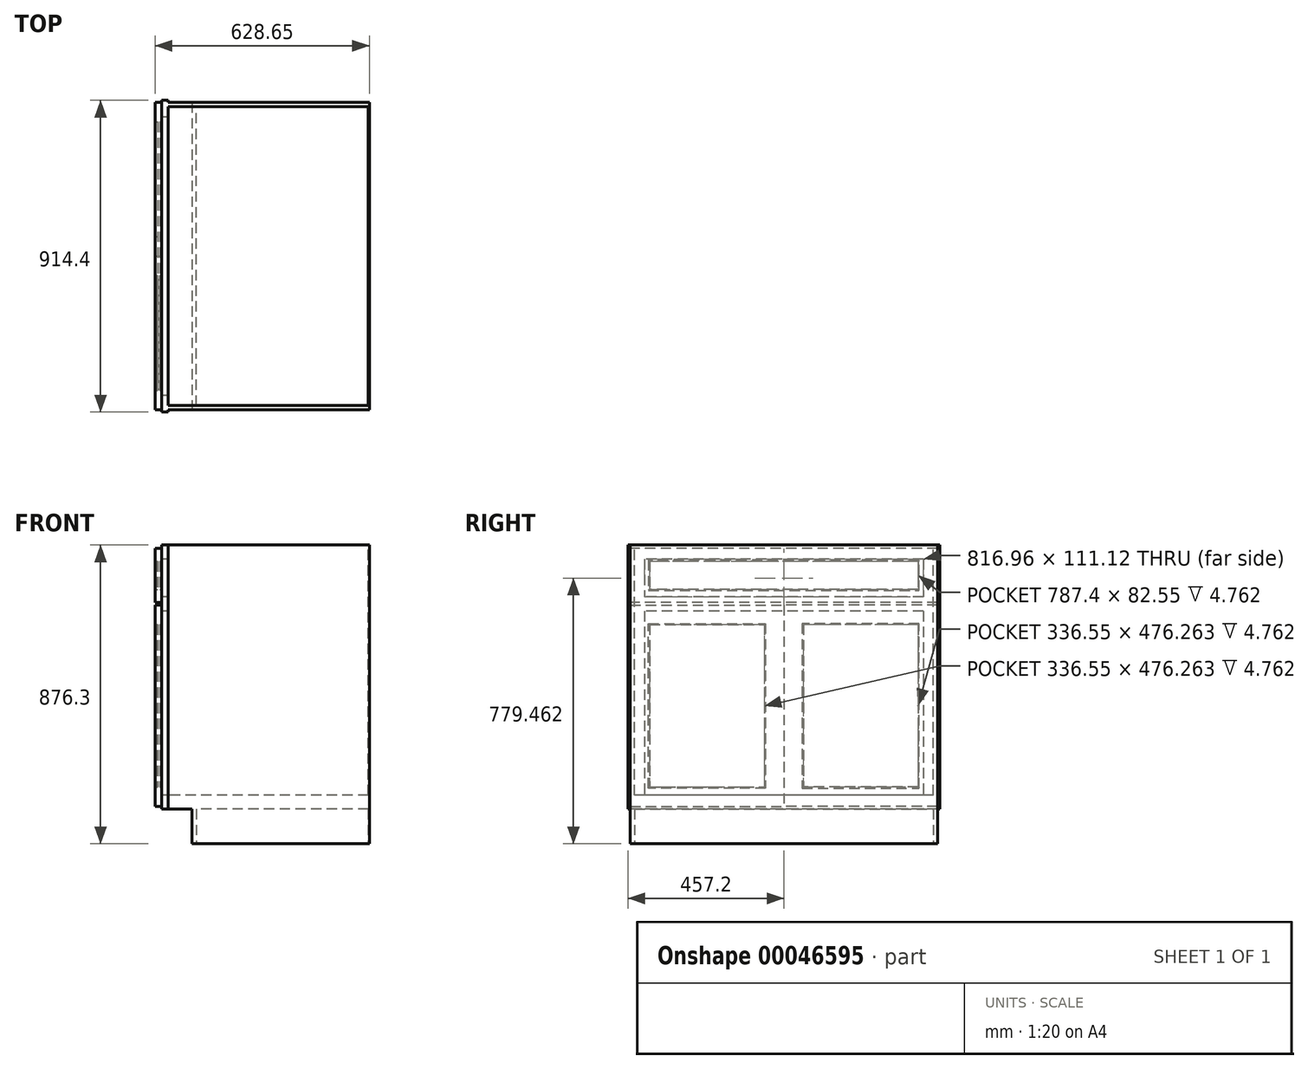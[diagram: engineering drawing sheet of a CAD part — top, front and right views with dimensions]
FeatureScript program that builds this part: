
annotation { "Feature Type Name" : "Feature", "Feature Type Description" : "" }
export const myFeature = defineFeature(function(context is Context, id is Id, definition is map)
    precondition{}
    {
        {
            var Q0;
            Q0=qCreatedBy(makeId("Front.planeOp"),FACE);
            var sketch = newSketch(context, id + "F0", { "sketchPlane" : qUnion([Q0])});
            skLineSegment(sketch, "E0.bottom", {"start": v(-304.8, -438.15) * mm, "end": v(304.8, -438.15) * mm});
            skLineSegment(sketch, "E0.top", {"start": v(-304.8, 438.15) * mm, "end": v(304.8, 438.15) * mm});
            skLineSegment(sketch, "E0.left", {"start": v(-304.8, -438.15) * mm, "end": v(-304.8, 438.15) * mm});
            skLineSegment(sketch, "E0.right", {"start": v(304.8, -438.15) * mm, "end": v(304.8, 438.15) * mm});
            skLineSegment(sketch, "E1", {"start": v(-304.8, -438.15) * mm, "end": v(304.8, 438.15) * mm, "construction": true});
            skSolve(sketch);
        }
        {
            var Q0;
            Q0=qSketchRegion(id+"F0",true);
            extrude(context, id + "F1", {"entities" : qUnion([Q0]), "oppositeDirection" : true, "depth" : 914.4 * mm});
        }
        {
            var Q0;
            Q0=makeQuery(id+"F1.opExtrude","CAP_FACE",FACE,{"disambiguationData":[OSD([sQuery(id+"F0.wireOp",EDGE,"E0.bottom"),sQuery(id+"F0.wireOp",EDGE,"E0.top"),sQuery(id+"F0.wireOp",EDGE,"E0.left"),sQuery(id+"F0.wireOp",EDGE,"E0.right")])],"isStart":true});
            var sketch = newSketch(context, id + "F2", { "sketchPlane" : qUnion([Q0])});
            skLineSegment(sketch, "E2.bottom", {"start": v(-304.8, -438.15) * mm, "end": v(-215.9, -438.15) * mm});
            skLineSegment(sketch, "E2.top", {"start": v(-304.8, -336.55) * mm, "end": v(-215.9, -336.55) * mm});
            skLineSegment(sketch, "E2.left", {"start": v(-304.8, -438.15) * mm, "end": v(-304.8, -336.55) * mm});
            skLineSegment(sketch, "E2.right", {"start": v(-215.9, -438.15) * mm, "end": v(-215.9, -336.55) * mm});
            skSolve(sketch);
        }
        {
            var Q0;
            Q0=qSketchRegion(id+"F2",true);
            extrude(context, id + "F3", {"entities" : qUnion([Q0]), "operationType" : NewBodyOperationType.REMOVE, "endBound" : BoundingType.THROUGH_ALL, "oppositeDirection" : true, "depth" : 25.4 * mm});
        }
        {
            var Q0;
            Q0=makeQuery(id+"F1.opExtrude","SWEPT_FACE",FACE,{"disambiguationData":[OSD([sQuery(id+"F0.wireOp",EDGE,"E0.left")])]});
            var sketch = newSketch(context, id + "F4", { "sketchPlane" : qUnion([Q0])});
            skLineSegment(sketch, "E3.bottom", {"start": v(-865.68, 396.88) * mm, "end": v(-48.72, 396.88) * mm});
            skLineSegment(sketch, "E3.top", {"start": v(-865.68, -295.28) * mm, "end": v(-48.72, -295.28) * mm});
            skLineSegment(sketch, "E3.left", {"start": v(-865.68, 396.88) * mm, "end": v(-865.68, -295.28) * mm});
            skLineSegment(sketch, "E3.right", {"start": v(-48.72, 396.88) * mm, "end": v(-48.72, -295.28) * mm});
            skLineSegment(sketch, "E4", {"start": v(-914.4, 438.15) * mm, "end": v(0, -336.55) * mm, "construction": true});
            skSolve(sketch);
        }
        {
            var Q0;
            Q0=qSketchRegion(id+"F4",true);
            extrude(context, id + "F5", {"entities" : qUnion([Q0]), "operationType" : NewBodyOperationType.REMOVE, "oppositeDirection" : true, "depth" : 19.05 * mm});
        }
        {
            var Q0;
            Q0=makeQuery(id+"F1.opExtrude","SWEPT_FACE",FACE,{"disambiguationData":[OSD([sQuery(id+"F0.wireOp",EDGE,"E0.top")])]});
            var sketch = newSketch(context, id + "F6", { "sketchPlane" : qUnion([Q0])});
            skLineSegment(sketch, "E5.bottom", {"start": v(304.8, 914.4) * mm, "end": v(-285.75, 914.4) * mm});
            skLineSegment(sketch, "E5.top", {"start": v(304.8, 908.05) * mm, "end": v(-285.75, 908.05) * mm});
            skLineSegment(sketch, "E5.left", {"start": v(304.8, 914.4) * mm, "end": v(304.8, 908.05) * mm});
            skLineSegment(sketch, "E5.right", {"start": v(-285.75, 914.4) * mm, "end": v(-285.75, 908.05) * mm});
            skLineSegment(sketch, "E6.bottom", {"start": v(304.8, 0) * mm, "end": v(-285.75, 0) * mm});
            skLineSegment(sketch, "E6.top", {"start": v(304.8, 6.35) * mm, "end": v(-285.75, 6.35) * mm});
            skLineSegment(sketch, "E6.left", {"start": v(304.8, 0) * mm, "end": v(304.8, 6.35) * mm});
            skLineSegment(sketch, "E6.right", {"start": v(-285.75, 0) * mm, "end": v(-285.75, 6.35) * mm});
            skSolve(sketch);
        }
        {
            var Q0;
            Q0=qSketchRegion(id+"F6",true);
            extrude(context, id + "F7", {"entities" : qUnion([Q0]), "operationType" : NewBodyOperationType.REMOVE, "endBound" : BoundingType.THROUGH_ALL, "oppositeDirection" : true, "depth" : 25.4 * mm});
        }
        {
            var Q0;
            Q0=makeQuery(id+"F1.opExtrude","SWEPT_FACE",FACE,{"disambiguationData":[OSD([sQuery(id+"F0.wireOp",EDGE,"E0.top")])]});
            var sketch = newSketch(context, id + "F8", { "sketchPlane" : qUnion([Q0])});
            skLineSegment(sketch, "E7.bottom", {"start": v(301.62, 895.35) * mm, "end": v(-285.75, 895.35) * mm});
            skLineSegment(sketch, "E7.top", {"start": v(301.63, 19.05) * mm, "end": v(-285.75, 19.05) * mm});
            skLineSegment(sketch, "E7.left", {"start": v(301.62, 895.35) * mm, "end": v(301.63, 19.05) * mm});
            skLineSegment(sketch, "E7.right", {"start": v(-285.75, 895.35) * mm, "end": v(-285.75, 19.05) * mm});
            skSolve(sketch);
        }
        {
            var Q0;
            Q0=qSketchRegion(id+"F8",true);
            var Q1;
            Q1=makeQuery(id+"F5.boolean.opBoolean","COPY",FACE,{"derivedFrom":makeQuery(id+"F5.opExtrude","SWEPT_FACE",FACE,{"disambiguationData":[OSD([sQuery(id+"F4.wireOp",EDGE,"E3.top")])]})});
            extrude(context, id + "F9", {"entities" : qUnion([Q0]), "operationType" : NewBodyOperationType.REMOVE, "endBound" : BoundingType.UP_TO_SURFACE, "oppositeDirection" : true, "endBoundEntityFace" : qUnion([Q1]), "depth" : 25.4 * mm});
        }
        {
            var Q0;
            Q0=makeQuery(id+"F1.opExtrude","SWEPT_FACE",FACE,{"disambiguationData":[OSD([sQuery(id+"F0.wireOp",EDGE,"E0.left")])]});
            var sketch = newSketch(context, id + "F10", { "sketchPlane" : qUnion([Q0])});
            skLineSegment(sketch, "E8.bottom", {"start": v(-865.68, 285.75) * mm, "end": v(-48.72, 285.75) * mm});
            skLineSegment(sketch, "E8.top", {"start": v(-865.68, 244.47) * mm, "end": v(-48.72, 244.47) * mm});
            skLineSegment(sketch, "E8.left", {"start": v(-865.68, 285.75) * mm, "end": v(-865.68, 244.47) * mm});
            skLineSegment(sketch, "E8.right", {"start": v(-48.72, 285.75) * mm, "end": v(-48.72, 244.47) * mm});
            skSolve(sketch);
        }
        {
            var Q0;
            Q0=qSketchRegion(id+"F10",true);
            var Q1;
            Q1=makeQuery(id+"F9.boolean.opBoolean","COPY",FACE,{"derivedFrom":makeQuery(id+"F9.opExtrude","SWEPT_FACE",FACE,{"disambiguationData":[OSD([sQuery(id+"F8.wireOp",EDGE,"E7.right")])]})});
            extrude(context, id + "F11", {"entities" : qUnion([Q0]), "operationType" : NewBodyOperationType.ADD, "endBound" : BoundingType.UP_TO_SURFACE, "oppositeDirection" : true, "endBoundEntityFace" : qUnion([Q1]), "depth" : 25.4 * mm});
        }
        {
            var Q0;
            Q0=makeQuery(id+"F11.boolean.opBoolean","MERGE",FACE,{"derivedFrom":[makeQuery(id+"F1.opExtrude","SWEPT_FACE",FACE,{"disambiguationData":[OSD([sQuery(id+"F0.wireOp",EDGE,"E0.left")])]}),makeQuery(id+"F11.opExtrude","CAP_FACE",FACE,{"disambiguationData":[OSD([sQuery(id+"F10.wireOp",EDGE,"E8.bottom"),sQuery(id+"F10.wireOp",EDGE,"E8.top"),sQuery(id+"F10.wireOp",EDGE,"E8.left"),sQuery(id+"F10.wireOp",EDGE,"E8.right")])],"isStart":true})]});
            var sketch = newSketch(context, id + "F12", { "sketchPlane" : qUnion([Q0])});
            skLineSegment(sketch, "E9.bottom", {"start": v(-908.05, 261.95) * mm, "end": v(-457.2, 261.95) * mm});
            skLineSegment(sketch, "E9.top", {"start": v(-908.05, -328.61) * mm, "end": v(-457.2, -328.61) * mm});
            skLineSegment(sketch, "E9.left", {"start": v(-908.05, 261.95) * mm, "end": v(-908.05, -328.61) * mm});
            skLineSegment(sketch, "E9.right", {"start": v(-457.2, 261.95) * mm, "end": v(-457.2, -328.61) * mm});
            skLineSegment(sketch, "E10.bottom", {"start": v(-850.9, 204.8) * mm, "end": v(-514.35, 204.8) * mm});
            skLineSegment(sketch, "E10.top", {"start": v(-850.9, -271.46) * mm, "end": v(-514.35, -271.46) * mm});
            skLineSegment(sketch, "E10.left", {"start": v(-850.9, 204.8) * mm, "end": v(-850.9, -271.46) * mm});
            skLineSegment(sketch, "E10.right", {"start": v(-514.35, 204.8) * mm, "end": v(-514.35, -271.46) * mm});
            skLineSegment(sketch, "E11", {"start": v(-457.2, 244.47) * mm, "end": v(-457.2, -295.28) * mm, "construction": true});
            skSolve(sketch);
        }
        {
            var Q0;
            Q0=qSketchRegion(id+"F12",true);
            extrude(context, id + "F13", {"entities" : qUnion([Q0]), "depth" : 19.05 * mm});
        }
        {
            var Q0;
            Q0=makeQuery(id+"F13.opExtrude","SWEPT_FACE",FACE,{"disambiguationData":[OSD([sQuery(id+"F12.wireOp",EDGE,"E10.top")])]});
            var sketch = newSketch(context, id + "F14", { "sketchPlane" : qUnion([Q0])});
            skLineSegment(sketch, "E12.bottom", {"start": v(-315.91, 850.9) * mm, "end": v(-309.56, 850.9) * mm});
            skLineSegment(sketch, "E12.top", {"start": v(-315.91, 514.35) * mm, "end": v(-309.56, 514.35) * mm});
            skLineSegment(sketch, "E12.left", {"start": v(-315.91, 850.9) * mm, "end": v(-315.91, 514.35) * mm});
            skLineSegment(sketch, "E12.right", {"start": v(-309.56, 850.9) * mm, "end": v(-309.56, 514.35) * mm});
            skSolve(sketch);
        }
        {
            var Q0;
            Q0=qSketchRegion(id+"F14",true);
            extrude(context, id + "F15", {"entities" : qUnion([Q0]), "operationType" : NewBodyOperationType.ADD, "endBound" : BoundingType.UP_TO_NEXT, "depth" : 25.4 * mm});
        }
        {
            var Q0;
            Q0=makeQuery(id+"F13.opExtrude","CAP_EDGE",EDGE,{"disambiguationData":[OSD([sQuery(id+"F12.wireOp",EDGE,"E10.left")])],"isStart":false});
            var Q1;
            Q1=makeQuery(id+"F13.opExtrude","CAP_EDGE",EDGE,{"disambiguationData":[OSD([sQuery(id+"F12.wireOp",EDGE,"E10.top")])],"isStart":false});
            var Q2;
            Q2=makeQuery(id+"F13.opExtrude","CAP_EDGE",EDGE,{"disambiguationData":[OSD([sQuery(id+"F12.wireOp",EDGE,"E10.right")])],"isStart":false});
            var Q3;
            Q3=makeQuery(id+"F13.opExtrude","CAP_EDGE",EDGE,{"disambiguationData":[OSD([sQuery(id+"F12.wireOp",EDGE,"E10.bottom")])],"isStart":false});
            chamfer(context, id + "F16", {"entities" : qUnion([Q0, Q1, Q2, Q3]), "width" : 3.17 * mm, "tangentPropagation" : true});
        }
        {
            var Q0;
            Q0=makeQuery(id+"F11.boolean.opBoolean","MERGE",FACE,{"derivedFrom":[makeQuery(id+"F1.opExtrude","SWEPT_FACE",FACE,{"disambiguationData":[OSD([sQuery(id+"F0.wireOp",EDGE,"E0.left")])]}),makeQuery(id+"F11.opExtrude","CAP_FACE",FACE,{"disambiguationData":[OSD([sQuery(id+"F10.wireOp",EDGE,"E8.bottom"),sQuery(id+"F10.wireOp",EDGE,"E8.top"),sQuery(id+"F10.wireOp",EDGE,"E8.left"),sQuery(id+"F10.wireOp",EDGE,"E8.right")])],"isStart":true})]});
            var sketch = newSketch(context, id + "F17", { "sketchPlane" : qUnion([Q0])});
            skLineSegment(sketch, "E13.bottom", {"start": v(-908.05, 428.62) * mm, "end": v(-6.35, 428.62) * mm});
            skLineSegment(sketch, "E13.top", {"start": v(-908.05, 269.88) * mm, "end": v(-6.35, 269.88) * mm});
            skLineSegment(sketch, "E13.left", {"start": v(-908.05, 428.62) * mm, "end": v(-908.05, 269.88) * mm});
            skLineSegment(sketch, "E13.right", {"start": v(-6.35, 428.63) * mm, "end": v(-6.35, 269.88) * mm});
            skLineSegment(sketch, "E14.bottom", {"start": v(-850.9, 390.52) * mm, "end": v(-63.5, 390.52) * mm});
            skLineSegment(sketch, "E14.top", {"start": v(-850.9, 307.98) * mm, "end": v(-63.5, 307.98) * mm});
            skLineSegment(sketch, "E14.left", {"start": v(-850.9, 390.52) * mm, "end": v(-850.9, 307.98) * mm});
            skLineSegment(sketch, "E14.right", {"start": v(-63.5, 390.53) * mm, "end": v(-63.5, 307.98) * mm});
            skSolve(sketch);
        }
        {
            var Q0;
            Q0=qSketchRegion(id+"F17",true);
            extrude(context, id + "F18", {"entities" : qUnion([Q0]), "depth" : 19.05 * mm});
        }
        {
            var Q0;
            Q0=makeQuery(id+"F18.opExtrude","SWEPT_FACE",FACE,{"disambiguationData":[OSD([sQuery(id+"F17.wireOp",EDGE,"E14.top")])]});
            var sketch = newSketch(context, id + "F19", { "sketchPlane" : qUnion([Q0])});
            skLineSegment(sketch, "E15.bottom", {"start": v(-309.56, 850.9) * mm, "end": v(-315.91, 850.9) * mm});
            skLineSegment(sketch, "E15.top", {"start": v(-309.56, 63.5) * mm, "end": v(-315.91, 63.5) * mm});
            skLineSegment(sketch, "E15.left", {"start": v(-309.56, 850.9) * mm, "end": v(-309.56, 63.5) * mm});
            skLineSegment(sketch, "E15.right", {"start": v(-315.91, 850.9) * mm, "end": v(-315.91, 63.5) * mm});
            skSolve(sketch);
        }
        {
            var Q0;
            Q0=qSketchRegion(id+"F19",true);
            var Q1;
            Q1=makeQuery(id+"F18.opExtrude","SWEPT_FACE",FACE,{"disambiguationData":[OSD([sQuery(id+"F17.wireOp",EDGE,"E14.bottom")])]});
            extrude(context, id + "F20", {"entities" : qUnion([Q0]), "operationType" : NewBodyOperationType.ADD, "endBound" : BoundingType.UP_TO_SURFACE, "endBoundEntityFace" : qUnion([Q1]), "depth" : 25.4 * mm});
        }
        {
            var Q0;
            Q0=makeQuery(id+"F18.opExtrude","CAP_EDGE",EDGE,{"disambiguationData":[OSD([sQuery(id+"F17.wireOp",EDGE,"E14.top")])],"isStart":false});
            var Q1;
            Q1=makeQuery(id+"F18.opExtrude","CAP_EDGE",EDGE,{"disambiguationData":[OSD([sQuery(id+"F17.wireOp",EDGE,"E14.left")])],"isStart":false});
            var Q2;
            Q2=makeQuery(id+"F18.opExtrude","CAP_EDGE",EDGE,{"disambiguationData":[OSD([sQuery(id+"F17.wireOp",EDGE,"E14.bottom")])],"isStart":false});
            var Q3;
            Q3=makeQuery(id+"F18.opExtrude","CAP_EDGE",EDGE,{"disambiguationData":[OSD([sQuery(id+"F17.wireOp",EDGE,"E14.right")])],"isStart":false});
            chamfer(context, id + "F21", {"entities" : qUnion([Q0, Q1, Q2, Q3]), "width" : 3.17 * mm, "tangentPropagation" : true});
        }
        {
            var Q0;
            Q0=makeQuery(id+"F1.opExtrude","SWEPT_FACE",FACE,{"disambiguationData":[OSD([sQuery(id+"F0.wireOp",EDGE,"E0.bottom")])]});
            var sketch = newSketch(context, id + "F22", { "sketchPlane" : qUnion([Q0])});
            skLineSegment(sketch, "E16.bottom", {"start": v(301.63, -19.05) * mm, "end": v(-203.2, -19.05) * mm});
            skLineSegment(sketch, "E16.top", {"start": v(301.63, -895.35) * mm, "end": v(-203.2, -895.35) * mm});
            skLineSegment(sketch, "E16.left", {"start": v(301.63, -19.05) * mm, "end": v(301.63, -895.35) * mm});
            skLineSegment(sketch, "E16.right", {"start": v(-203.2, -19.05) * mm, "end": v(-203.2, -895.35) * mm});
            skSolve(sketch);
        }
        {
            var Q0;
            Q0=qSketchRegion(id+"F22",true);
            extrude(context, id + "F23", {"entities" : qUnion([Q0]), "operationType" : NewBodyOperationType.REMOVE, "oppositeDirection" : true, "depth" : 101.6 * mm});
        }
        {
            var Q0;
            Q0=makeQuery(id+"F13.opExtrude","SWEPT_BODY",BODY,{"disambiguationData":[OSD([sQuery(id+"F12.wireOp",EDGE,"E9.bottom"),sQuery(id+"F12.wireOp",EDGE,"E9.top"),sQuery(id+"F12.wireOp",EDGE,"E9.left"),sQuery(id+"F12.wireOp",EDGE,"E9.right"),sQuery(id+"F12.wireOp",EDGE,"E10.bottom"),sQuery(id+"F12.wireOp",EDGE,"E10.top"),sQuery(id+"F12.wireOp",EDGE,"E10.left"),sQuery(id+"F12.wireOp",EDGE,"E10.right")])]});
            var Q1;
            Q1=makeQuery(id+"F13.opExtrude","SWEPT_FACE",FACE,{"disambiguationData":[OSD([sQuery(id+"F12.wireOp",EDGE,"E9.right")])]});
            mirror(context, id + "F24", {"entities" : qUnion([Q0]), "mirrorPlane" : qUnion([Q1])});
        }
    });
